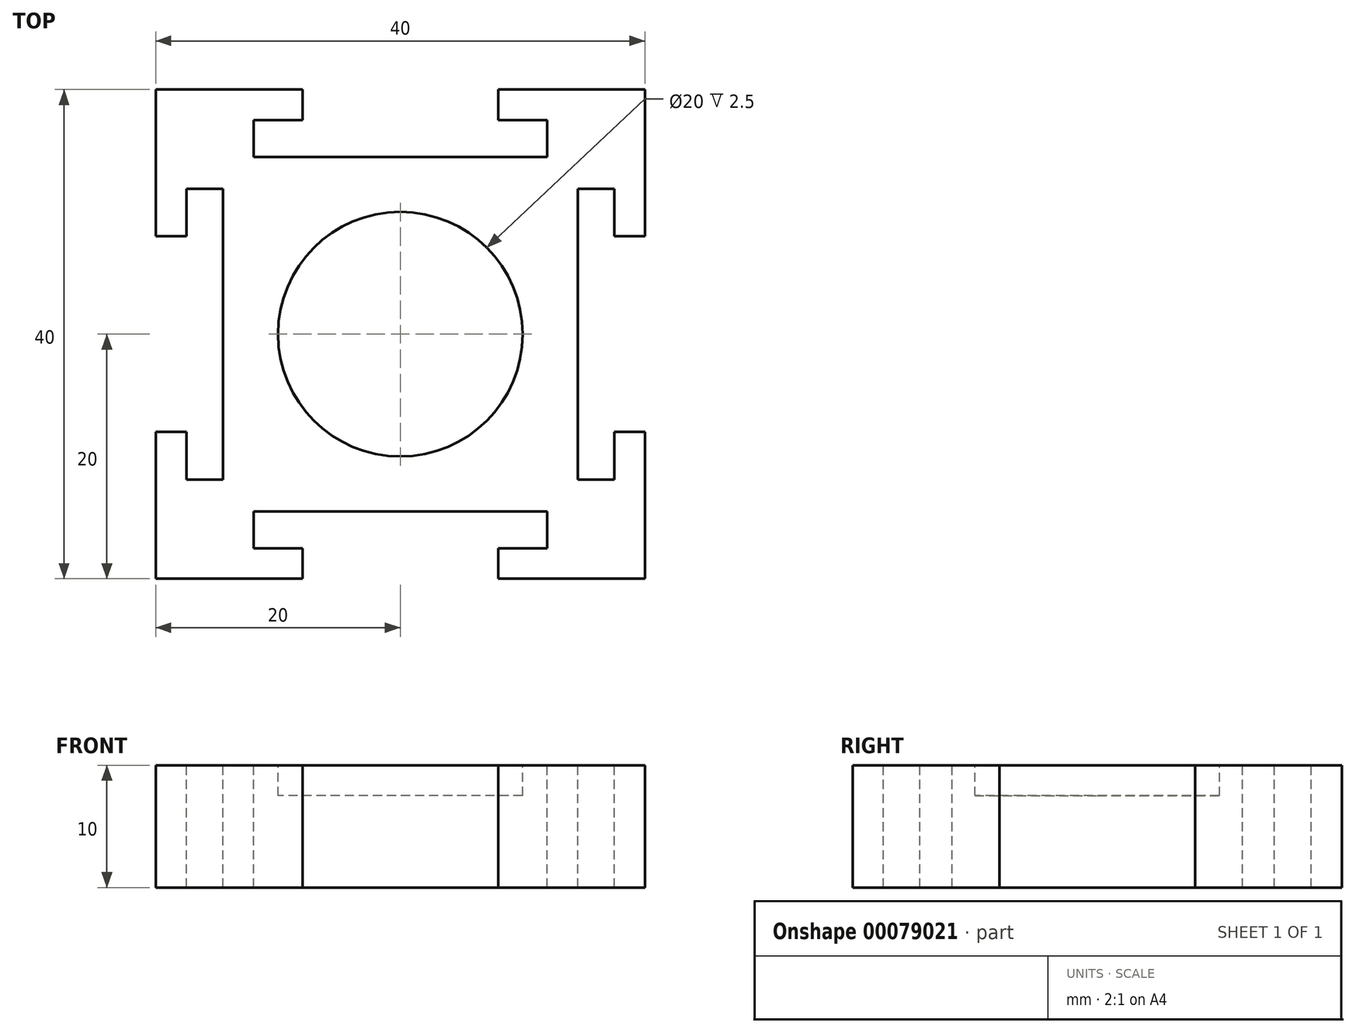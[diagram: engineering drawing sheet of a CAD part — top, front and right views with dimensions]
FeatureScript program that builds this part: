
annotation { "Feature Type Name" : "Feature", "Feature Type Description" : "" }
export const myFeature = defineFeature(function(context is Context, id is Id, definition is map)
    precondition{}
    {
        {
            var Q0;
            Q0=qCreatedBy(makeId("Top.planeOp"),FACE);
            var sketch = newSketch(context, id + "F0", { "sketchPlane" : qUnion([Q0])});
            skLineSegment(sketch, "E0.bottom", {"start": v(0, 20) * mm, "end": v(-20, 20) * mm});
            skLineSegment(sketch, "E0.right", {"start": v(-20, 20) * mm, "end": v(-20, 0) * mm});
            skPoint(sketch, "E0.middle", {"position": v(0, 0) * mm});
            skLineSegment(sketch, "E1.MirrorCS", {"start": v(-20, 0) * mm, "end": v(-20, 20) * mm});
            skPoint(sketch, "E2", {"position": v(-20, 0) * mm});
            skLineSegment(sketch, "E3", {"start": v(0, 20) * mm, "end": v(0, 0) * mm});
            skLineSegment(sketch, "E4", {"start": v(-20, 0) * mm, "end": v(0, 0) * mm});
            skPoint(sketch, "E0.left.end.orphan", {"position": v(20, -20) * mm});
            skPoint(sketch, "E0.left.start.orphan", {"position": v(20, 20) * mm});
            skPoint(sketch, "E5.orphan", {"position": v(-20, -20) * mm});
            skLineSegment(sketch, "E6.MirrorCS", {"start": v(-17.5, 11.88) * mm, "end": v(-14.5, 11.88) * mm});
            skLineSegment(sketch, "E7.MirrorCS", {"start": v(-14.5, 11.88) * mm, "end": v(-14.5, -0.12) * mm});
            skLineSegment(sketch, "E8.MirrorCS", {"start": v(-20, 8) * mm, "end": v(-17.5, 8) * mm});
            skLineSegment(sketch, "E9.MirrorCS", {"start": v(-12, 17.5) * mm, "end": v(0, 17.5) * mm});
            skLineSegment(sketch, "E10.MirrorCS", {"start": v(0, 14.5) * mm, "end": v(0, 20) * mm});
            skLineSegment(sketch, "E11.MirrorCS", {"start": v(-8, 20) * mm, "end": v(-8, 17.5) * mm});
            skLineSegment(sketch, "E12.MirrorCS", {"start": v(-12, 14.5) * mm, "end": v(0, 14.5) * mm});
            skLineSegment(sketch, "E13.MirrorCS", {"start": v(-12, 17.5) * mm, "end": v(-12, 14.5) * mm});
            skLineSegment(sketch, "E14", {"start": v(-17.5, 11.88) * mm, "end": v(-17.5, 0) * mm});
            skSolve(sketch);
        }
        {
            var Q0;
            {var subQ11=sQuery(id+"F0.wireOp",EDGE,"E6.MirrorCS");Q0=makeQuery(id+"F0.imprint","IMPRINT",FACE,{"disambiguationData":[TD([[makeQuery(id+"F0.imprint","IMPRINT",EDGE,{"derivedFrom":subQ11}),1.0]])]});}
            extrude(context, id + "F1", {"entities" : qUnion([Q0]), "oppositeDirection" : true, "depth" : 10 * mm});
        }
        {
            var Q0;
            Q0=makeQuery(id+"F1.opExtrude","CAP_FACE",FACE,{"disambiguationData":[OSD([sQuery(id+"F0.wireOp",EDGE,"E0.bottom"),sQuery(id+"F0.wireOp",EDGE,"UIb6YOiN-wxSo-lSF2-kpko-APr7q6lGE7w8"),sQuery(id+"F0.wireOp",EDGE,"7sIu6wZ2-w2ZO-qvAv-kVXd-9A4nwvC2tgGi.bottom"),sQuery(id+"F0.wireOp",EDGE,"7sIu6wZ2-w2ZO-qvAv-kVXd-9A4nwvC2tgGi.top"),sQuery(id+"F0.wireOp",EDGE,"7sIu6wZ2-w2ZO-qvAv-kVXd-9A4nwvC2tgGi.left"),sQuery(id+"F0.wireOp",EDGE,"E1.MirrorCS"),sQuery(id+"F0.wireOp",EDGE,"XQsER0wi-Vg6o-c3ds-G2QR-Lw313FhJWP8Z"),sQuery(id+"F0.wireOp",EDGE,"E3"),sQuery(id+"F0.wireOp",EDGE,"E4"),sQuery(id+"F0.wireOp",EDGE,"omr1NIdk-LD6w-flbd-csqk-4ex0jU9YYlC1"),sQuery(id+"F0.wireOp",EDGE,"QZpuFEbT-zwrV-33dt-xeFp-y3lYNh4AIB55"),sQuery(id+"F0.wireOp",EDGE,"HOiBXv6H-g9ta-x4qK-dGRR-ioPKnYE1xfiL"),sQuery(id+"F0.wireOp",EDGE,"MHQost7p-gHpg-h2Aw-RlJn-Fn5qbKcMKlH5"),sQuery(id+"F0.wireOp",EDGE,"FmDu4MX8-r8PL-tAcH-PEms-lTVrpWOdV1De")])],"isStart":true});
            var sketch = newSketch(context, id + "F2", { "sketchPlane" : qUnion([Q0])});
            skArc(sketch, "E15", {"start": v(0, 10) * mm, "mid": v(-7.07, 7.07) * mm, "end": v(-10, 0) * mm});
            skPoint(sketch, "E16", {"position": v(0, 10) * mm});
            skPoint(sketch, "E17", {"position": v(-10, 0) * mm});
            skLineSegment(sketch, "E18", {"start": v(0, 10) * mm, "end": v(0, 0) * mm});
            skLineSegment(sketch, "E19", {"start": v(0, 0) * mm, "end": v(-10, 0) * mm});
            skSolve(sketch);
        }
        {
            var Q0;
            Q0=qSketchRegion(id+"F2",true);
            extrude(context, id + "F3", {"entities" : qUnion([Q0]), "operationType" : NewBodyOperationType.REMOVE, "oppositeDirection" : true, "depth" : 2.5 * mm});
        }
        {
            var Q0;
            Q0=makeQuery(id+"F1.opExtrude","SWEPT_BODY",BODY,{"disambiguationData":[OSD([sQuery(id+"F0.wireOp",EDGE,"E0.bottom"),sQuery(id+"F0.wireOp",EDGE,"UIb6YOiN-wxSo-lSF2-kpko-APr7q6lGE7w8"),sQuery(id+"F0.wireOp",EDGE,"7sIu6wZ2-w2ZO-qvAv-kVXd-9A4nwvC2tgGi.bottom"),sQuery(id+"F0.wireOp",EDGE,"7sIu6wZ2-w2ZO-qvAv-kVXd-9A4nwvC2tgGi.top"),sQuery(id+"F0.wireOp",EDGE,"7sIu6wZ2-w2ZO-qvAv-kVXd-9A4nwvC2tgGi.left"),sQuery(id+"F0.wireOp",EDGE,"E1.MirrorCS"),sQuery(id+"F0.wireOp",EDGE,"XQsER0wi-Vg6o-c3ds-G2QR-Lw313FhJWP8Z"),sQuery(id+"F0.wireOp",EDGE,"E3"),sQuery(id+"F0.wireOp",EDGE,"E4")])]});
            var Q1;
            Q1=qCreatedBy(makeId("Right.planeOp"),FACE);
            mirror(context, id + "F4", {"operationType" : NewBodyOperationType.ADD, "entities" : qUnion([Q0]), "mirrorPlane" : qUnion([Q1])});
        }
        {
            var Q0;
            Q0=makeQuery(id+"F1.opExtrude","SWEPT_BODY",BODY,{"disambiguationData":[OSD([sQuery(id+"F0.wireOp",EDGE,"E0.bottom"),sQuery(id+"F0.wireOp",EDGE,"UIb6YOiN-wxSo-lSF2-kpko-APr7q6lGE7w8"),sQuery(id+"F0.wireOp",EDGE,"7sIu6wZ2-w2ZO-qvAv-kVXd-9A4nwvC2tgGi.bottom"),sQuery(id+"F0.wireOp",EDGE,"7sIu6wZ2-w2ZO-qvAv-kVXd-9A4nwvC2tgGi.top"),sQuery(id+"F0.wireOp",EDGE,"7sIu6wZ2-w2ZO-qvAv-kVXd-9A4nwvC2tgGi.left"),sQuery(id+"F0.wireOp",EDGE,"E1.MirrorCS"),sQuery(id+"F0.wireOp",EDGE,"XQsER0wi-Vg6o-c3ds-G2QR-Lw313FhJWP8Z"),sQuery(id+"F0.wireOp",EDGE,"E3"),sQuery(id+"F0.wireOp",EDGE,"E4")])]});
            var Q1;
            Q1=qCreatedBy(makeId("Front.planeOp"),FACE);
            mirror(context, id + "F5", {"operationType" : NewBodyOperationType.ADD, "entities" : qUnion([Q0]), "mirrorPlane" : qUnion([Q1])});
        }
    });
